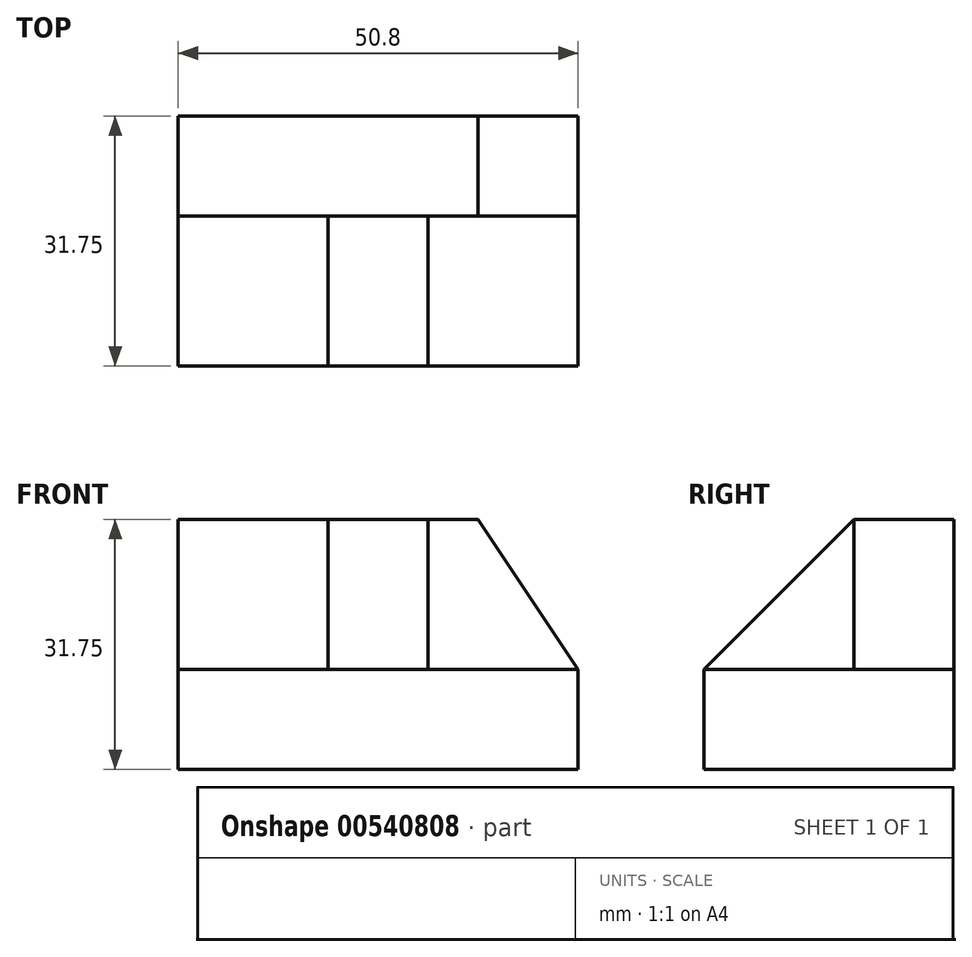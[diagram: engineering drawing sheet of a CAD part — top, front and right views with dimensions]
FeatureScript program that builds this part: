
annotation { "Feature Type Name" : "Feature", "Feature Type Description" : "" }
export const myFeature = defineFeature(function(context is Context, id is Id, definition is map)
    precondition{}
    {
        {
            var Q0;
            Q0=qCreatedBy(makeId("Front.planeOp"),FACE);
            var sketch = newSketch(context, id + "F0", { "sketchPlane" : qUnion([Q0])});
            skLineSegment(sketch, "E0", {"start": v(0, 0) * mm, "end": v(0, 31.75) * mm});
            skLineSegment(sketch, "E1", {"start": v(0, 31.75) * mm, "end": v(50.8, 31.75) * mm});
            skLineSegment(sketch, "E2", {"start": v(50.8, 31.75) * mm, "end": v(50.8, 0) * mm});
            skLineSegment(sketch, "E3", {"start": v(50.8, 0) * mm, "end": v(0, 0) * mm});
            skSolve(sketch);
        }
        {
            var Q0;
            Q0=makeQuery(id+"F0.imprint","IMPRINT",FACE,{"disambiguationData":[TD([[makeQuery(id+"F0.imprint","IMPRINT",EDGE,{"derivedFrom":sQuery(id+"F0.wireOp",EDGE,"E0")}),-1.0]])]});
            extrude(context, id + "F1", {"entities" : qUnion([Q0]), "depth" : 31.75 * mm, "offsetDistance" : 25.4 * mm});
        }
        {
            var Q0;
            Q0=makeQuery(id+"F1.opExtrude","CAP_FACE",FACE,{"disambiguationData":[OSD([sQuery(id+"F0.wireOp",EDGE,"E0"),sQuery(id+"F0.wireOp",EDGE,"E1"),sQuery(id+"F0.wireOp",EDGE,"E2"),sQuery(id+"F0.wireOp",EDGE,"E3")])],"isStart":false});
            var sketch = newSketch(context, id + "F2", { "sketchPlane" : qUnion([Q0])});
            skLineSegment(sketch, "E4", {"start": v(0, 12.7) * mm, "end": v(19.05, 12.7) * mm});
            skLineSegment(sketch, "E5", {"start": v(19.05, 12.7) * mm, "end": v(19.05, 31.75) * mm});
            skLineSegment(sketch, "E6", {"start": v(19.05, 31.75) * mm, "end": v(0, 31.75) * mm});
            skLineSegment(sketch, "E7", {"start": v(0, 31.75) * mm, "end": v(0, 12.7) * mm});
            skSolve(sketch);
        }
        {
            var Q0;
            Q0=makeQuery(id+"F2.imprint","IMPRINT",FACE,{"disambiguationData":[TD([[makeQuery(id+"F2.imprint","IMPRINT",EDGE,{"derivedFrom":sQuery(id+"F2.wireOp",EDGE,"E4")}),1.0]])]});
            extrude(context, id + "F3", {"entities" : qUnion([Q0]), "operationType" : NewBodyOperationType.REMOVE, "oppositeDirection" : true, "depth" : 19.05 * mm, "offsetDistance" : 25.4 * mm});
        }
        {
            var Q0;
            Q0=makeQuery(id+"F1.opExtrude","CAP_FACE",FACE,{"disambiguationData":[OSD([sQuery(id+"F0.wireOp",EDGE,"E0"),sQuery(id+"F0.wireOp",EDGE,"E1"),sQuery(id+"F0.wireOp",EDGE,"E2"),sQuery(id+"F0.wireOp",EDGE,"E3")])],"isStart":false});
            var sketch = newSketch(context, id + "F4", { "sketchPlane" : qUnion([Q0])});
            skLineSegment(sketch, "E8", {"start": v(50.8, 12.7) * mm, "end": v(31.75, 12.7) * mm});
            skLineSegment(sketch, "E9", {"start": v(31.75, 12.7) * mm, "end": v(31.75, 31.75) * mm});
            skLineSegment(sketch, "E10", {"start": v(31.75, 31.75) * mm, "end": v(50.8, 31.75) * mm});
            skLineSegment(sketch, "E11", {"start": v(50.8, 31.75) * mm, "end": v(50.8, 12.7) * mm});
            skSolve(sketch);
        }
        {
            var Q0;
            Q0=makeQuery(id+"F4.imprint","IMPRINT",FACE,{"disambiguationData":[TD([[makeQuery(id+"F4.imprint","IMPRINT",EDGE,{"derivedFrom":sQuery(id+"F4.wireOp",EDGE,"E8")}),-1.0]])]});
            extrude(context, id + "F5", {"entities" : qUnion([Q0]), "operationType" : NewBodyOperationType.REMOVE, "oppositeDirection" : true, "depth" : 19.05 * mm, "offsetDistance" : 25.4 * mm});
        }
        {
            var Q0;
            Q0=makeQuery(id+"F5.boolean.opBoolean","COPY",FACE,{"derivedFrom":makeQuery(id+"F5.opExtrude","SWEPT_FACE",FACE,{"disambiguationData":[OSD([sQuery(id+"F4.wireOp",EDGE,"E9")])]})});
            var sketch = newSketch(context, id + "F6", { "sketchPlane" : qUnion([Q0])});
            skLineSegment(sketch, "E12", {"start": v(-12.7, 31.75) * mm, "end": v(-31.75, 12.7) * mm});
            skLineSegment(sketch, "E13", {"start": v(-31.75, 12.7) * mm, "end": v(-31.75, 31.75) * mm});
            skLineSegment(sketch, "E14", {"start": v(-31.75, 31.75) * mm, "end": v(-12.7, 31.75) * mm});
            skSolve(sketch);
        }
        {
            var Q0;
            Q0=makeQuery(id+"F6.imprint","IMPRINT",FACE,{"disambiguationData":[TD([[makeQuery(id+"F6.imprint","IMPRINT",EDGE,{"derivedFrom":sQuery(id+"F6.wireOp",EDGE,"E12")}),-1.0]])]});
            extrude(context, id + "F7", {"entities" : qUnion([Q0]), "operationType" : NewBodyOperationType.REMOVE, "oppositeDirection" : true, "depth" : 12.7 * mm, "offsetDistance" : 25.4 * mm});
        }
        {
            var Q0;
            Q0=makeQuery(id+"F5.boolean.opBoolean","COPY",FACE,{"derivedFrom":makeQuery(id+"F5.opExtrude","CAP_FACE",FACE,{"disambiguationData":[OSD([sQuery(id+"F4.wireOp",EDGE,"E8"),sQuery(id+"F4.wireOp",EDGE,"E9"),sQuery(id+"F4.wireOp",EDGE,"E10"),sQuery(id+"F4.wireOp",EDGE,"E11")])],"isStart":false})});
            var sketch = newSketch(context, id + "F8", { "sketchPlane" : qUnion([Q0])});
            skLineSegment(sketch, "E15", {"start": v(38.1, 31.75) * mm, "end": v(50.8, 12.7) * mm});
            skLineSegment(sketch, "E16", {"start": v(50.8, 12.7) * mm, "end": v(50.8, 31.75) * mm});
            skLineSegment(sketch, "E17", {"start": v(50.8, 31.75) * mm, "end": v(38.1, 31.75) * mm});
            skSolve(sketch);
        }
        {
            var Q0;
            Q0=makeQuery(id+"F8.imprint","IMPRINT",FACE,{"disambiguationData":[TD([[makeQuery(id+"F8.imprint","IMPRINT",EDGE,{"derivedFrom":sQuery(id+"F8.wireOp",EDGE,"E15")}),1.0]])]});
            extrude(context, id + "F9", {"entities" : qUnion([Q0]), "operationType" : NewBodyOperationType.REMOVE, "oppositeDirection" : true, "depth" : 12.7 * mm, "offsetDistance" : 25.4 * mm});
        }
    });
